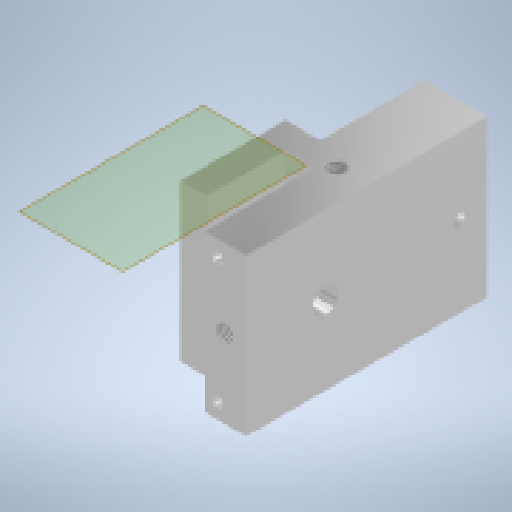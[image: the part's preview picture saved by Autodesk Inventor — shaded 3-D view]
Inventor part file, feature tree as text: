
AUTODESK INVENTOR PART (.ipt)
format: ipt  version: 2025 (Build 290162010, 162A)  size: 244,736 bytes
history: native  units: mm
features: sketch x10, reference x10, hole x8, other x6, projected_geometry x3, extrude x2, plane x1
ambient origin geometry x8: Origin, YZ Plane, XZ Plane, XY Plane, X Axis, Y Axis, Z Axis, Center Point
bodies: Volumenkörper1 (feature_tree)
feature tree (40):
  plane  "Arbeitsebene1"
  extrude  "Extrusion1"  Depth=5.0mm
  sketch  "Skizze2"  dims[d2=5.0mm d3=13.0mm]
  hole  "Katzeverbindung"  [1 undecoded]
  hole  "Zentrierbolzen"  [1 undecoded]
  hole  "seilV"  [1 undecoded]
  hole  "GLVV"  [1 undecoded]
  hole  "GLVO"  [1 undecoded]
  hole  "GLVU"  [1 undecoded]
  hole  "DLVU"  [1 undecoded]
  hole  "DLVO"  [1 undecoded]
  extrude  "Extrusion2"  Depth=1.0mm
  sketch  "Skizze1"  dims[d0=20.0mm d1=5.0mm]
  reference  "Referenz1"
  reference  "Referenz2"
  reference  "Referenz3"
  reference  "Referenz4"
  sketch  "Skizze3"  dims[d4=30.0mm d5=0.0mm d6=5.0mm]
  reference  "Referenz5"
  sketch  "Skizze4"  dims[d18=12.0mm]
  reference  "Referenz6"
  reference  "Referenz7"
  sketch  "Skizze5"  dims[d28=3.242mm d29=8.0mm d30=7.4mm d31=15.0mm d32=90.0deg d33=11.8mm d34=20.594885mm]
  sketch  "Skizze6"  dims[d35=2.0mm d36=6.0mm d37=4.0mm d38=2.0mm d39=90.0deg d40=6.0mm d41=20.594885mm]
  projected_geometry  "Projizierte Kontur2"
  sketch  "Skizze7"  dims[d45=3.242mm d46=9.0mm d47=4.0mm d48=2.0mm d49=90.0deg d50=8.0mm d51=20.594885mm]
  reference  "Referenz8"
  projected_geometry  "Projizierte Kontur3"
  sketch  "Skizze8"  dims[d54=1.567mm d55=2.5mm d56=4.0mm d57=2.0mm d58=90.0deg d59=4.0mm d60=20.594885mm d62=9.0mm]
  projected_geometry  "Projizierte Kontur4"
  reference  "Referenz9"
  sketch  "Skizze9"  dims[d63=1.567mm d64=2.5mm d65=4.0mm d66=2.0mm d67=90.0deg d68=4.0mm d69=20.594885mm d70=4.0mm]
  reference  "Referenz10"
  sketch  "Skizze10"  dims[d71=1.567mm d72=2.5mm d73=4.0mm d74=2.0mm d75=90.0deg d76=4.0mm d77=20.594885mm d78=5.0mm d79=6.0mm d80=4.0mm d81=2.0mm d82=90.0deg d83=8.0mm d84=0.0mm d85=5.0mm d86=6.0mm d87=4.0mm d88=2.0mm d89=90.0deg d90=8.0mm d91=0.0mm d92=6.0mm d93=23.0mm d94=3.0mm d95=1.0mm d96=0.0mm d97=0.5mm d98=0.872665mm]
  other  "<userpath>\Documents\Inventor\Krandemonstrator\Demonstrator.iam"
  other  "Demonstrator.iam"
  other  "Träger:1"
  other  "Katze_Lagerhalter_hinten:1"
  other  "LagerVV:1"
  other  "LagerVO:1"
note: 8 required parameter values undecoded (feature->parameter linkage not recoverable at this tier; creation-order binding heuristic only, values carry confidence <= 0.55)
